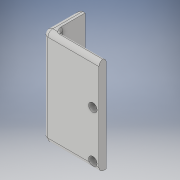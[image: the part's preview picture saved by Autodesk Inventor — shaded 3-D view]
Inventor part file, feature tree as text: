
AUTODESK INVENTOR PART (.ipt)
format: ipt  version: 2019.4 (Build 234330000, 330)  size: 222,720 bytes
history: native  units: mm
features: fillet x5, extrude x4, sketch x4, plane x1
ambient origin geometry x8: Origin, YZ Plane, XZ Plane, XY Plane, X Axis, Y Axis, Z Axis, Center Point
bodies: Solid1 (feature_tree)
feature tree (14):
  extrude  "Extrusion1"  Depth=3.0mm
  extrude  "Extrusion2"  Depth=3.0mm
  fillet  "Fillet1"  Radius=40.0mm
  fillet  "Fillet2"  Radius=2.5mm
  fillet  "Fillet3"  Radius=3.0mm
  extrude  "Extrusion3"  Depth=3.5mm
  plane  "Work Plane1"
  extrude  "Extrusion4"  TaperAngle=90.0deg  [1 undecoded]
  fillet  "Fillet4"  Radius=3.5mm
  fillet  "Fillet5"  Radius=3.0mm
  sketch  "Sketch1"  dims[d0=20.0mm d1=3.0mm]
  sketch  "Sketch2"  dims[d2=15.0mm d3=3.0mm d4=40.0mm d5=0.0mm d6=2.5mm d7=3.0mm]
  sketch  "Sketch3"  dims[d8=90.0deg d9=3.5mm]
  sketch  "Sketch4"  dims[d10=19.175mm d11=90.0deg d12=3.5mm d13=3.0mm d14=0.0mm d15=2.0mm d16=2.0mm d17=2.0mm d18=10.0mm d19=90.0deg d20=6.5mm d21=10.0mm d22=90.0deg d23=3.5mm d24=3.5mm d25=3.0mm d26=0.0mm d27=-22.0mm d30=12.0mm d31=3.0mm d32=0.0mm d33=2.5mm d34=2.5mm]
note: 1 required parameter value undecoded (feature->parameter linkage not recoverable at this tier; creation-order binding heuristic only, values carry confidence <= 0.55)
